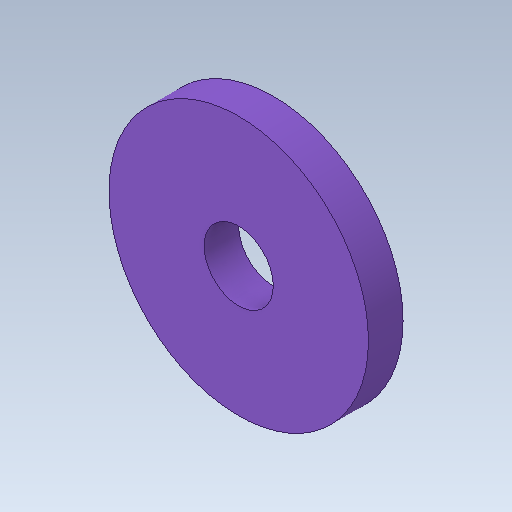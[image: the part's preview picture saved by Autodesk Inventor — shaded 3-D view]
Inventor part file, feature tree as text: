
AUTODESK INVENTOR PART (.ipt)
format: ipt  version: 2020 (Build 240168000, 168)  size: 96,768 bytes
history: native  units: mm
features: other x1, extrude x1, sketch x1
ambient origin geometry x8: Origin, YZ Plane, XZ Plane, XY Plane, X Axis, Y Axis, Z Axis, Center Point
bodies: Body1 (feature_tree)
feature tree (3):
  other  "Твердое тело1"
  extrude  "Выдавливание1"  Depth=15.0mm
  sketch  "Эскиз1"
